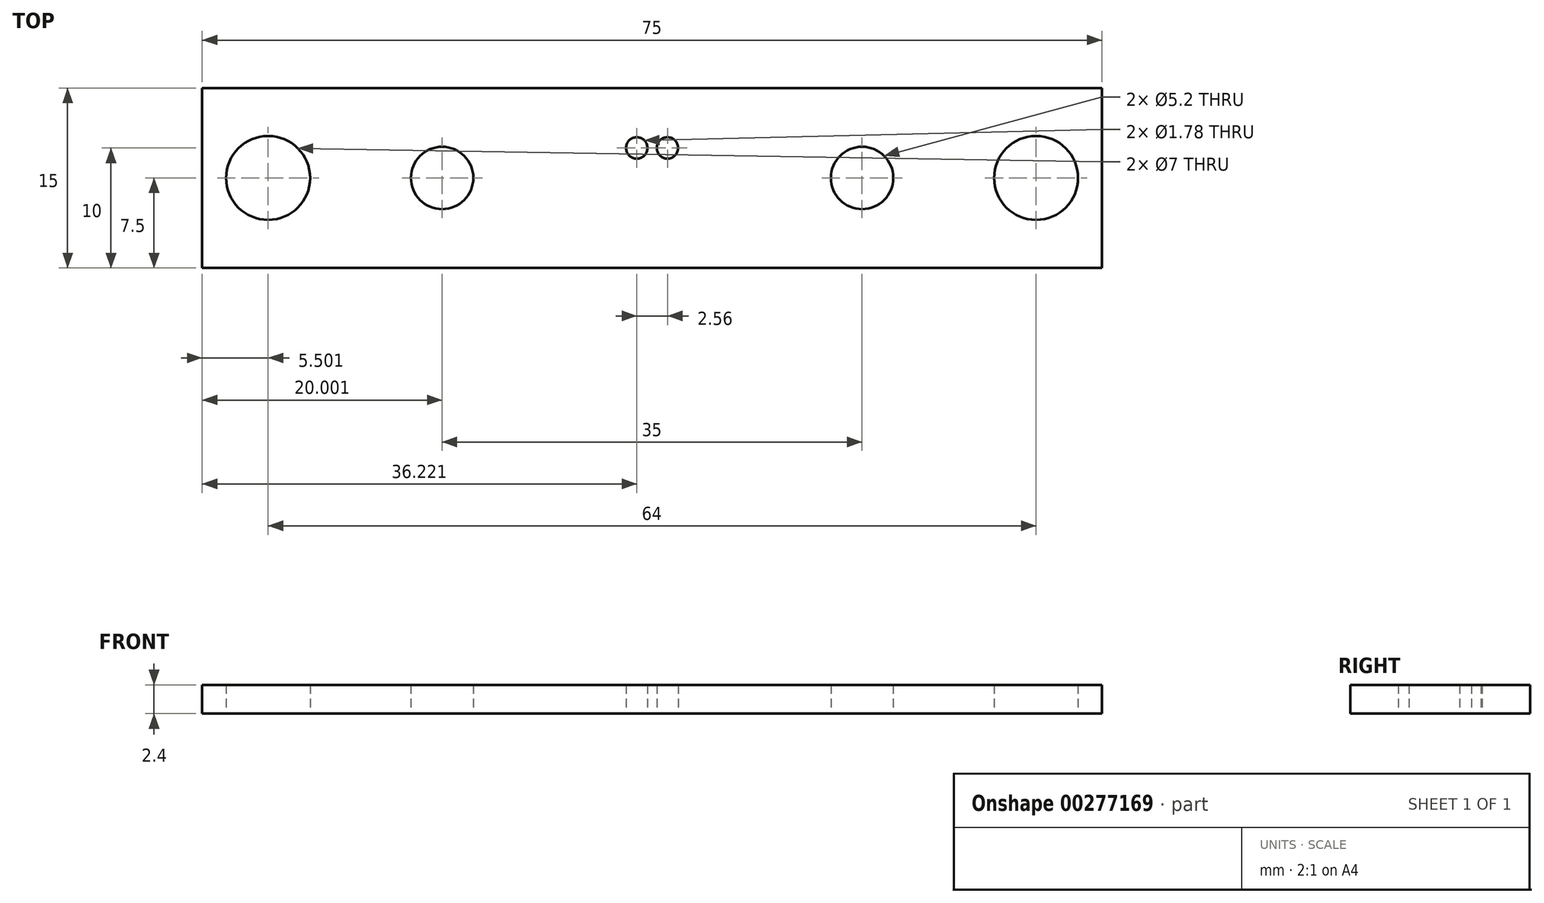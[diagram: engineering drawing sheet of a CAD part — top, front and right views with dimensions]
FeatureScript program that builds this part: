
annotation { "Feature Type Name" : "Feature", "Feature Type Description" : "" }
export const myFeature = defineFeature(function(context is Context, id is Id, definition is map)
    precondition{}
    {
        {
            var Q0;
            Q0=qCreatedBy(makeId("Top.planeOp"),FACE);
            var sketch = newSketch(context, id + "F0", { "sketchPlane" : qUnion([Q0])});
            skLineSegment(sketch, "E0.bottom", {"start": v(-69.69, 0) * mm, "end": v(5.31, 0) * mm});
            skLineSegment(sketch, "E0.top", {"start": v(-69.69, -15) * mm, "end": v(5.31, -15) * mm});
            skLineSegment(sketch, "E0.left", {"start": v(-69.69, 0) * mm, "end": v(-69.69, -15) * mm});
            skLineSegment(sketch, "E0.right", {"start": v(5.31, 0) * mm, "end": v(5.31, -15) * mm});
            skCircle(sketch, "E1", {"center": v(-49.69, -7.5) * mm, "radius": 2.6 * mm});
            skCircle(sketch, "E2", {"center": v(-64.19, -7.5) * mm, "radius": 3.5 * mm});
            skCircle(sketch, "E3", {"center": v(-33.47, -5) * mm, "radius": 0.89 * mm});
            skLineSegment(sketch, "E4", {"start": v(-32.19, 0) * mm, "end": v(-32.19, -15) * mm});
            skCircle(sketch, "E5.MirrorC", {"center": v(-30.9, -5) * mm, "radius": 0.89 * mm});
            skCircle(sketch, "E6.MirrorC", {"center": v(-14.69, -7.5) * mm, "radius": 2.6 * mm});
            skCircle(sketch, "E7.MirrorC", {"center": v(-0.19, -7.5) * mm, "radius": 3.5 * mm});
            skSolve(sketch);
        }
        {
            var Q0;
            {var subQ0=sQuery(id+"F0.wireOp",EDGE,"E0.left");Q0=makeQuery(id+"F0.imprint","IMPRINT",FACE,{"disambiguationData":[TD([[makeQuery(id+"F0.imprint","IMPRINT",EDGE,{"derivedFrom":subQ0}),1.0]])]});}
            var Q1;
            {var subQ1=sQuery(id+"F0.wireOp",EDGE,"E0.right");Q1=makeQuery(id+"F0.imprint","IMPRINT",FACE,{"disambiguationData":[TD([[makeQuery(id+"F0.imprint","IMPRINT",EDGE,{"derivedFrom":subQ1}),-1.0]])]});}
            extrude(context, id + "F1", {"entities" : qUnion([Q0, Q1]), "depth" : 2.4 * mm});
        }
    });
